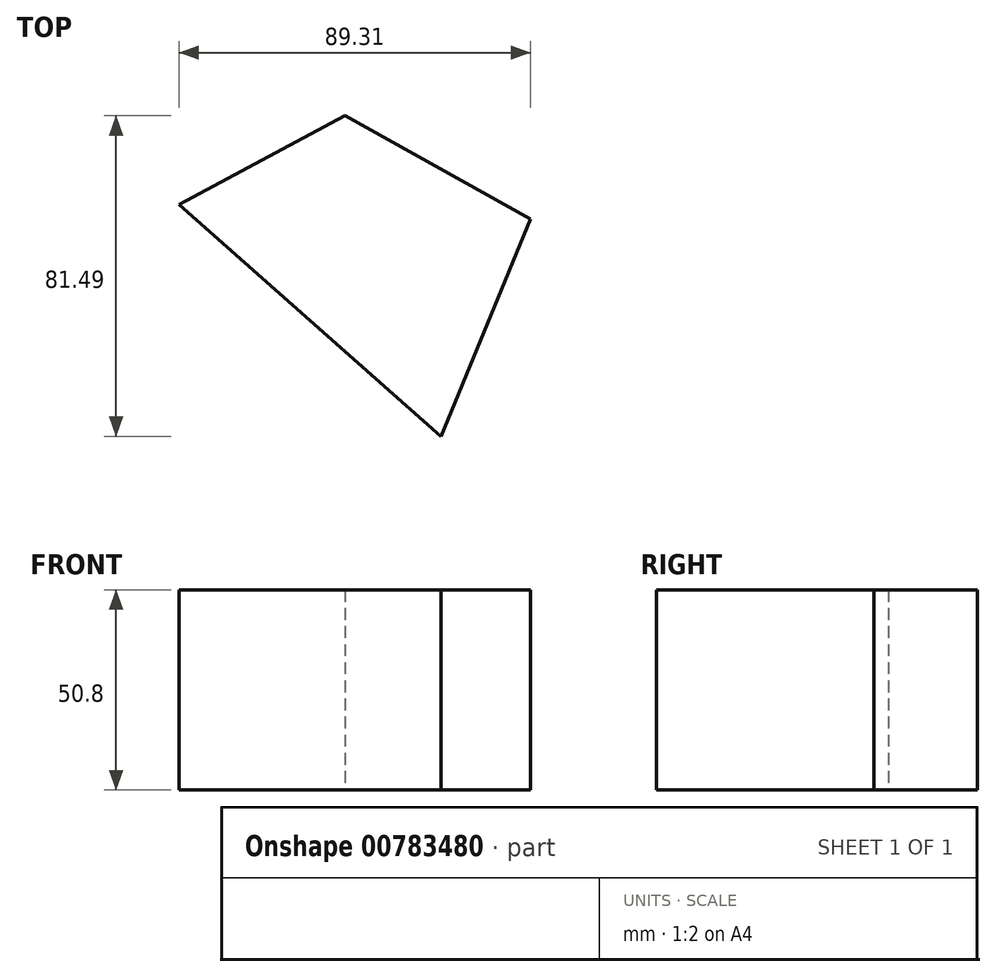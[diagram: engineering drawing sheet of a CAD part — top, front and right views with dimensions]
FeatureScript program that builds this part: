
annotation { "Feature Type Name" : "Feature", "Feature Type Description" : "" }
export const myFeature = defineFeature(function(context is Context, id is Id, definition is map)
    precondition{}
    {
        {
            var Q0;
            Q0=qCreatedBy(makeId("Top.planeOp"),FACE);
            var sketch = newSketch(context, id + "F0", { "sketchPlane" : qUnion([Q0])});
            skLineSegment(sketch, "E0", {"start": v(89.3, 22.4) * mm, "end": v(42.17, 48.64) * mm});
            skLineSegment(sketch, "E1", {"start": v(42.17, 48.64) * mm, "end": v(0, 26.1) * mm});
            skLineSegment(sketch, "E2", {"start": v(0, 26.1) * mm, "end": v(66.54, -32.85) * mm});
            skLineSegment(sketch, "E3", {"start": v(66.54, -32.85) * mm, "end": v(89.3, 22.4) * mm});
            skSolve(sketch);
        }
        {
            var Q0;
            Q0 = qSketchRegion(id + "F0", true);
            extrude(context, id + "F1", {"entities" : qUnion([Q0]), "depth" : 50.8 * mm, "offsetDistance" : 25.4 * mm});
        }
    });
